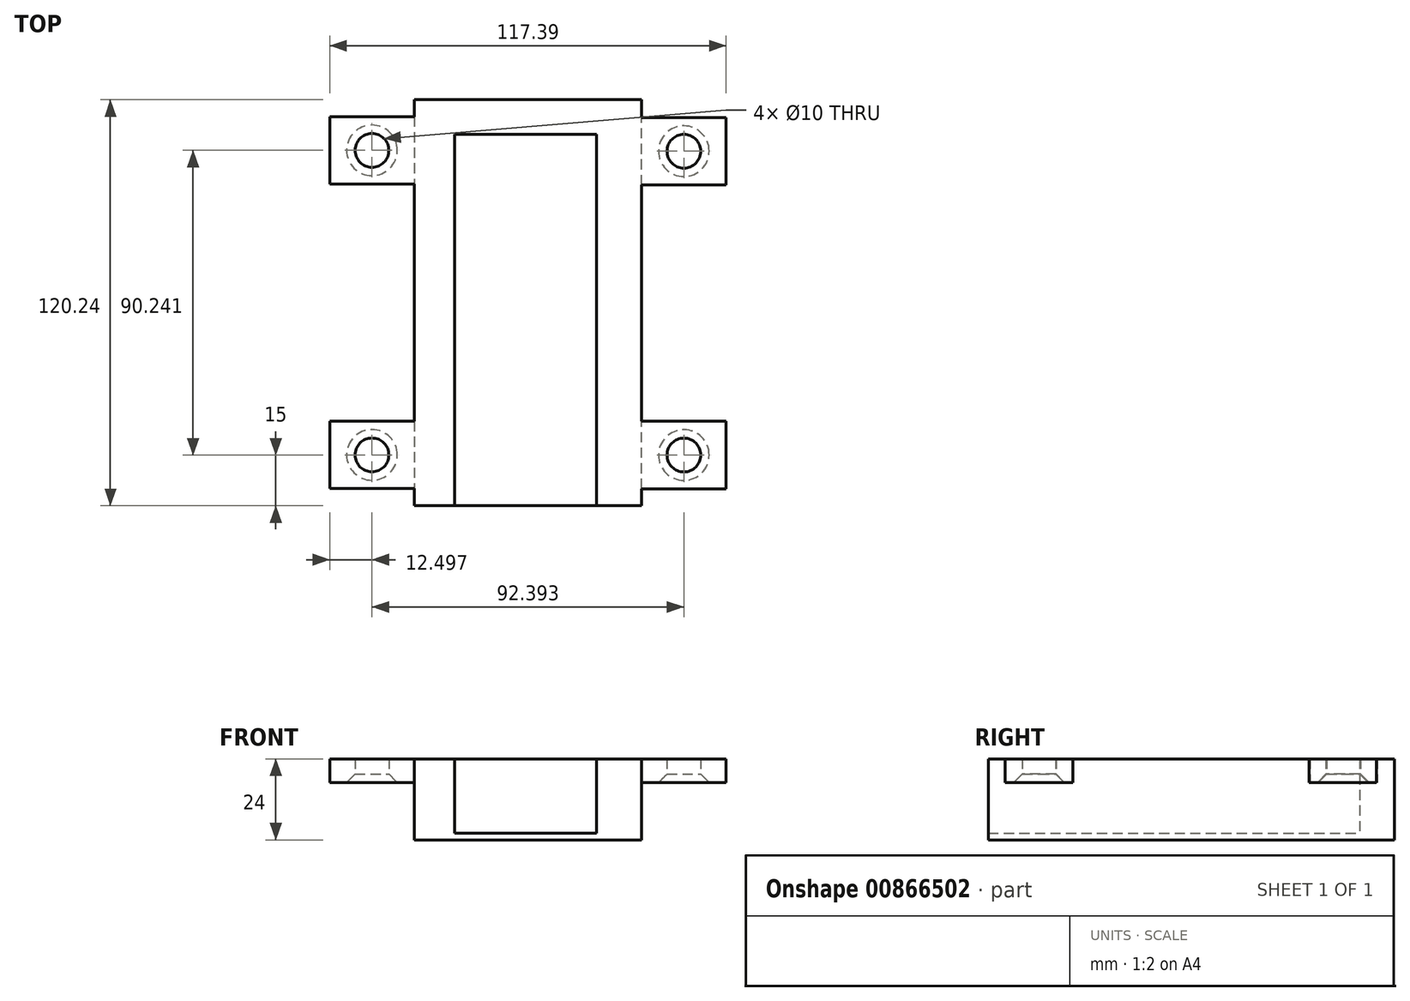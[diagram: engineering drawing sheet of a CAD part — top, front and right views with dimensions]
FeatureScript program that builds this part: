
annotation { "Feature Type Name" : "Feature", "Feature Type Description" : "" }
export const myFeature = defineFeature(function(context is Context, id is Id, definition is map)
    precondition{}
    {
        {
            var Q0;
            Q0=qCreatedBy(makeId("Top.planeOp"),FACE);
            var sketch = newSketch(context, id + "F0", { "sketchPlane" : qUnion([Q0])});
            skLineSegment(sketch, "E0.bottom", {"start": v(0, 0) * mm, "end": v(42, 0) * mm});
            skLineSegment(sketch, "E0.top", {"start": v(0, 110) * mm, "end": v(42, 110) * mm});
            skLineSegment(sketch, "E0.left", {"start": v(0, 0) * mm, "end": v(0, 110) * mm});
            skLineSegment(sketch, "E0.right", {"start": v(42, 0) * mm, "end": v(42, 110) * mm});
            skLineSegment(sketch, "E1.top", {"start": v(-12, 120.24) * mm, "end": v(55.39, 120.24) * mm});
            skLineSegment(sketch, "E1.left", {"start": v(-12, 0) * mm, "end": v(-12, 120.24) * mm});
            skLineSegment(sketch, "E1.right", {"start": v(55.39, 0) * mm, "end": v(55.39, 120.24) * mm});
            skPoint(sketch, "E1.middle", {"position": v(21.7, 54.61) * mm});
            skLineSegment(sketch, "E2", {"start": v(-12, 0) * mm, "end": v(55.39, 0) * mm});
            skPoint(sketch, "E3.orphan", {"position": v(-12, -11.02) * mm});
            skPoint(sketch, "E4.orphan", {"position": v(55.39, -11.02) * mm});
            skSolve(sketch);
        }
        {
            var Q0;
            Q0=makeQuery(id+"F0.imprint","IMPRINT",FACE,{"disambiguationData":[TD([[makeQuery(id+"F0.imprint","IMPRINT",EDGE,{"derivedFrom":sQuery(id+"F0.wireOp",EDGE,"E0.top")}),1.0]])]});
            extrude(context, id + "F1", {"entities" : qUnion([Q0]), "depth" : 22 * mm, "offsetDistance" : 25 * mm});
        }
        {
            var Q0;
            Q0 = qSketchRegion(id + "F0", true);
            extrude(context, id + "F2", {"entities" : qUnion([Q0]), "operationType" : NewBodyOperationType.ADD, "oppositeDirection" : true, "depth" : 2 * mm, "offsetDistance" : 25 * mm});
        }
        {
            var Q0;
            {var subQ0=sQuery(id+"F0.wireOp",EDGE,"E1.right");Q0=makeQuery(id+"F2.boolean.opBoolean","MERGE",FACE,{"derivedFrom":[makeQuery(id+"F1.opExtrude","SWEPT_FACE",FACE,{"disambiguationData":[OSD([subQ0])]}),makeQuery(id+"F2.opExtrude","SWEPT_FACE",FACE,{"disambiguationData":[OSD([subQ0])]})]});}
            var sketch = newSketch(context, id + "F3", { "sketchPlane" : qUnion([Q0])});
            skLineSegment(sketch, "E5", {"start": v(115.24, 22) * mm, "end": v(115.24, -2) * mm, "construction": true});
            skPoint(sketch, "E6", {"position": v(5, 22) * mm});
            skPoint(sketch, "E7", {"position": v(115.24, 17) * mm});
            skPoint(sketch, "E8.oppositeSnap0", {"position": v(5, 15) * mm});
            skLineSegment(sketch, "E8.bottom", {"start": v(5, 22) * mm, "end": v(25, 22) * mm});
            skLineSegment(sketch, "E8.left", {"start": v(5, 22) * mm, "end": v(5, 15) * mm});
            skLineSegment(sketch, "E8.right", {"start": v(25, 22) * mm, "end": v(25, 15) * mm});
            skLineSegment(sketch, "E9", {"start": v(5, 15) * mm, "end": v(25, 15) * mm});
            skLineSegment(sketch, "E10.2.0.0", {"start": v(95, 22) * mm, "end": v(95, 15) * mm});
            skLineSegment(sketch, "E10.2.0.1", {"start": v(95, 15) * mm, "end": v(115, 15) * mm});
            skLineSegment(sketch, "E10.2.0.2", {"start": v(115, 22) * mm, "end": v(115, 15) * mm});
            skLineSegment(sketch, "E10.2.0.3", {"start": v(95, 22) * mm, "end": v(115, 22) * mm});
            skSolve(sketch);
        }
        {
            var Q0;
            Q0=makeQuery(id+"F3.imprint","IMPRINT",FACE,{"disambiguationData":[TD([[makeQuery(id+"F3.imprint","IMPRINT",EDGE,{"derivedFrom":sQuery(id+"F3.wireOp",EDGE,"E8.bottom")}),-1.0]])]});
            var Q1;
            Q1=makeQuery(id+"F3.imprint","IMPRINT",FACE,{"disambiguationData":[TD([[makeQuery(id+"F3.imprint","IMPRINT",EDGE,{"derivedFrom":sQuery(id+"F3.wireOp",EDGE,"E10.2.0.0")}),1.0]])]});
            extrude(context, id + "F4", {"entities" : qUnion([Q0, Q1]), "operationType" : NewBodyOperationType.ADD, "depth" : 25 * mm, "offsetDistance" : 25 * mm});
        }
        {
            var Q0;
            Q0=makeQuery(id+"F4.boolean.opBoolean","MERGE",FACE,{"derivedFrom":[makeQuery(id+"F1.opExtrude","CAP_FACE",FACE,{"disambiguationData":[OSD([sQuery(id+"F0.wireOp",EDGE,"E0.top"),sQuery(id+"F0.wireOp",EDGE,"E0.left"),sQuery(id+"F0.wireOp",EDGE,"E0.right"),sQuery(id+"F0.wireOp",EDGE,"E1.top"),sQuery(id+"F0.wireOp",EDGE,"E1.left"),sQuery(id+"F0.wireOp",EDGE,"E1.right"),sQuery(id+"F0.wireOp",EDGE,"E2")])],"isStart":false}),makeQuery(id+"F4.opExtrude","SWEPT_FACE",FACE,{"disambiguationData":[OSD([sQuery(id+"F3.wireOp",EDGE,"E8.bottom")])]}),makeQuery(id+"F4.opExtrude","SWEPT_FACE",FACE,{"disambiguationData":[OSD([sQuery(id+"F3.wireOp",EDGE,"E10.2.0.3")])]})]});
            var sketch = newSketch(context, id + "F5", { "sketchPlane" : qUnion([Q0])});
            skLineSegment(sketch, "E11", {"start": v(55.39, 115) * mm, "end": v(55.39, 5) * mm, "construction": true});
            skSolve(sketch);
        }
        {
            var Q0;
            {var subQ0=sQuery(id+"F0.wireOp",EDGE,"E1.left");Q0=makeQuery(id+"F2.boolean.opBoolean","MERGE",FACE,{"derivedFrom":[makeQuery(id+"F1.opExtrude","SWEPT_FACE",FACE,{"disambiguationData":[OSD([subQ0])]}),makeQuery(id+"F2.opExtrude","SWEPT_FACE",FACE,{"disambiguationData":[OSD([subQ0])]})]});}
            var sketch = newSketch(context, id + "F6", { "sketchPlane" : qUnion([Q0])});
            skLineSegment(sketch, "E12", {"start": v(-115.24, 22) * mm, "end": v(-115.24, 15) * mm});
            skLineSegment(sketch, "E13.bottom", {"start": v(-115.24, 22) * mm, "end": v(-95.24, 22) * mm});
            skLineSegment(sketch, "E13.top", {"start": v(-115.24, 15) * mm, "end": v(-95.24, 15) * mm});
            skLineSegment(sketch, "E13.right", {"start": v(-95.24, 22) * mm, "end": v(-95.24, 15) * mm});
            skLineSegment(sketch, "E14.1.0.3", {"start": v(-70.14, 22) * mm, "end": v(-50.14, 22) * mm});
            skLineSegment(sketch, "E14.2.0.0", {"start": v(-25.04, 22) * mm, "end": v(-25.04, 15) * mm});
            skLineSegment(sketch, "E14.2.0.1", {"start": v(-25.04, 15) * mm, "end": v(-5.04, 15) * mm});
            skLineSegment(sketch, "E14.2.0.2", {"start": v(-5.04, 22) * mm, "end": v(-5.04, 15) * mm});
            skLineSegment(sketch, "E14.2.0.3", {"start": v(-25.04, 22) * mm, "end": v(-5.04, 22) * mm});
            skLineSegment(sketch, "E14.direction1", {"start": v(-115.24, 15) * mm, "end": v(-95.24, 15) * mm, "construction": true});
            skSolve(sketch);
        }
        {
            var Q0;
            Q0=makeQuery(id+"F6.imprint","IMPRINT",FACE,{"disambiguationData":[TD([[makeQuery(id+"F6.imprint","IMPRINT",EDGE,{"derivedFrom":sQuery(id+"F6.wireOp",EDGE,"E13.bottom")}),1.0]])]});
            var Q1;
            Q1=makeQuery(id+"F6.imprint","IMPRINT",FACE,{"disambiguationData":[TD([[makeQuery(id+"F6.imprint","IMPRINT",EDGE,{"derivedFrom":sQuery(id+"F6.wireOp",EDGE,"E14.2.0.0")}),1.0]])]});
            extrude(context, id + "F7", {"entities" : qUnion([Q0, Q1]), "operationType" : NewBodyOperationType.ADD, "depth" : 25 * mm, "offsetDistance" : 25 * mm});
        }
        {
            var Q0;
            Q0=makeQuery(id+"F4.opExtrude","SWEPT_FACE",FACE,{"disambiguationData":[OSD([sQuery(id+"F3.wireOp",EDGE,"E10.2.0.1")])]});
            var sketch = newSketch(context, id + "F8", { "sketchPlane" : qUnion([Q0])});
            skLineSegment(sketch, "E15", {"start": v(80.39, -105) * mm, "end": v(55.39, -105) * mm, "construction": true});
            skPoint(sketch, "E16", {"position": v(67.89, -105) * mm});
            skSolve(sketch);
        }
        {
            var Q0;
            Q0=sQuery(id+"F8.wireOp",VERTEX,"E16");
            var Q1;
            Q1=makeQuery(id+"F1.opExtrude","SWEPT_BODY",BODY,{"disambiguationData":[OSD([sQuery(id+"F0.wireOp",EDGE,"E0.top"),sQuery(id+"F0.wireOp",EDGE,"E0.left"),sQuery(id+"F0.wireOp",EDGE,"E0.right"),sQuery(id+"F0.wireOp",EDGE,"E1.top"),sQuery(id+"F0.wireOp",EDGE,"E1.left"),sQuery(id+"F0.wireOp",EDGE,"E1.right"),sQuery(id+"F0.wireOp",EDGE,"E2")])]});
            hole(context, id + "F9", {"style" : HoleStyle.C_SINK, "endStyle" : HoleEndStyle.THROUGH, "holeDiameter" : 10 * mm, "cSinkDiameter" : 15 * mm, "cSinkAngle" : 90 * degree, "majorDiameter" : 5 * mm, "isTappedThrough" : true, "tappedDepth" : 12 * mm, "tapClearance" : 3, "locations" : qUnion([Q0]), "scope" : qUnion([Q1])});
        }
        {
            var Q0;
            Q0=makeQuery(id+"F4.opExtrude","SWEPT_FACE",FACE,{"disambiguationData":[OSD([sQuery(id+"F3.wireOp",EDGE,"E9")])]});
            var sketch = newSketch(context, id + "F10", { "sketchPlane" : qUnion([Q0])});
            skLineSegment(sketch, "E17", {"start": v(80.39, -5) * mm, "end": v(55.39, -25) * mm, "construction": true});
            skPoint(sketch, "E18", {"position": v(67.89, -15) * mm});
            skSolve(sketch);
        }
        {
            var Q0;
            Q0=sQuery(id+"F10.wireOp",VERTEX,"E18");
            var Q1;
            Q1=makeQuery(id+"F1.opExtrude","SWEPT_BODY",BODY,{"disambiguationData":[OSD([sQuery(id+"F0.wireOp",EDGE,"E0.top"),sQuery(id+"F0.wireOp",EDGE,"E0.left"),sQuery(id+"F0.wireOp",EDGE,"E0.right"),sQuery(id+"F0.wireOp",EDGE,"E1.top"),sQuery(id+"F0.wireOp",EDGE,"E1.left"),sQuery(id+"F0.wireOp",EDGE,"E1.right"),sQuery(id+"F0.wireOp",EDGE,"E2")])]});
            hole(context, id + "F11", {"style" : HoleStyle.C_SINK, "endStyle" : HoleEndStyle.THROUGH, "holeDiameter" : 10 * mm, "cSinkDiameter" : 15 * mm, "cSinkAngle" : 90 * degree, "majorDiameter" : 5 * mm, "isTappedThrough" : true, "tappedDepth" : 12 * mm, "tapClearance" : 3, "locations" : qUnion([Q0]), "scope" : qUnion([Q1])});
        }
        {
            var Q0;
            Q0=makeQuery(id+"F7.opExtrude","SWEPT_FACE",FACE,{"disambiguationData":[OSD([sQuery(id+"F6.wireOp",EDGE,"E14.2.0.1")])]});
            var sketch = newSketch(context, id + "F12", { "sketchPlane" : qUnion([Q0])});
            skLineSegment(sketch, "E19", {"start": v(-37, -25.04) * mm, "end": v(-12, -5.04) * mm, "construction": true});
            skPoint(sketch, "E20", {"position": v(-24.5, -15.04) * mm});
            skSolve(sketch);
        }
        {
            var Q0;
            Q0=sQuery(id+"F12.wireOp",VERTEX,"E20");
            var Q1;
            Q1=makeQuery(id+"F1.opExtrude","SWEPT_BODY",BODY,{"disambiguationData":[OSD([sQuery(id+"F0.wireOp",EDGE,"E0.top"),sQuery(id+"F0.wireOp",EDGE,"E0.left"),sQuery(id+"F0.wireOp",EDGE,"E0.right"),sQuery(id+"F0.wireOp",EDGE,"E1.top"),sQuery(id+"F0.wireOp",EDGE,"E1.left"),sQuery(id+"F0.wireOp",EDGE,"E1.right"),sQuery(id+"F0.wireOp",EDGE,"E2")])]});
            hole(context, id + "F13", {"style" : HoleStyle.C_SINK, "endStyle" : HoleEndStyle.THROUGH, "holeDiameter" : 10 * mm, "cSinkDiameter" : 15 * mm, "cSinkAngle" : 90 * degree, "majorDiameter" : 5 * mm, "isTappedThrough" : true, "tappedDepth" : 12 * mm, "tapClearance" : 3, "locations" : qUnion([Q0]), "scope" : qUnion([Q1])});
        }
        {
            var Q0;
            Q0=makeQuery(id+"F7.opExtrude","SWEPT_FACE",FACE,{"disambiguationData":[OSD([sQuery(id+"F6.wireOp",EDGE,"E13.top")])]});
            var sketch = newSketch(context, id + "F14", { "sketchPlane" : qUnion([Q0])});
            skLineSegment(sketch, "E21", {"start": v(-37, -115.24) * mm, "end": v(-12, -95.24) * mm, "construction": true});
            skPoint(sketch, "E22", {"position": v(-24.5, -105.24) * mm});
            skSolve(sketch);
        }
        {
            var Q0;
            Q0=sQuery(id+"F14.wireOp",VERTEX,"E22");
            var Q1;
            Q1=makeQuery(id+"F1.opExtrude","SWEPT_BODY",BODY,{"disambiguationData":[OSD([sQuery(id+"F0.wireOp",EDGE,"E0.top"),sQuery(id+"F0.wireOp",EDGE,"E0.left"),sQuery(id+"F0.wireOp",EDGE,"E0.right"),sQuery(id+"F0.wireOp",EDGE,"E1.top"),sQuery(id+"F0.wireOp",EDGE,"E1.left"),sQuery(id+"F0.wireOp",EDGE,"E1.right"),sQuery(id+"F0.wireOp",EDGE,"E2")])]});
            hole(context, id + "F15", {"style" : HoleStyle.C_SINK, "endStyle" : HoleEndStyle.THROUGH, "holeDiameter" : 10 * mm, "cSinkDiameter" : 15 * mm, "cSinkAngle" : 90 * degree, "majorDiameter" : 5 * mm, "isTappedThrough" : true, "tappedDepth" : 12 * mm, "tapClearance" : 3, "locations" : qUnion([Q0]), "scope" : qUnion([Q1])});
        }
    });
